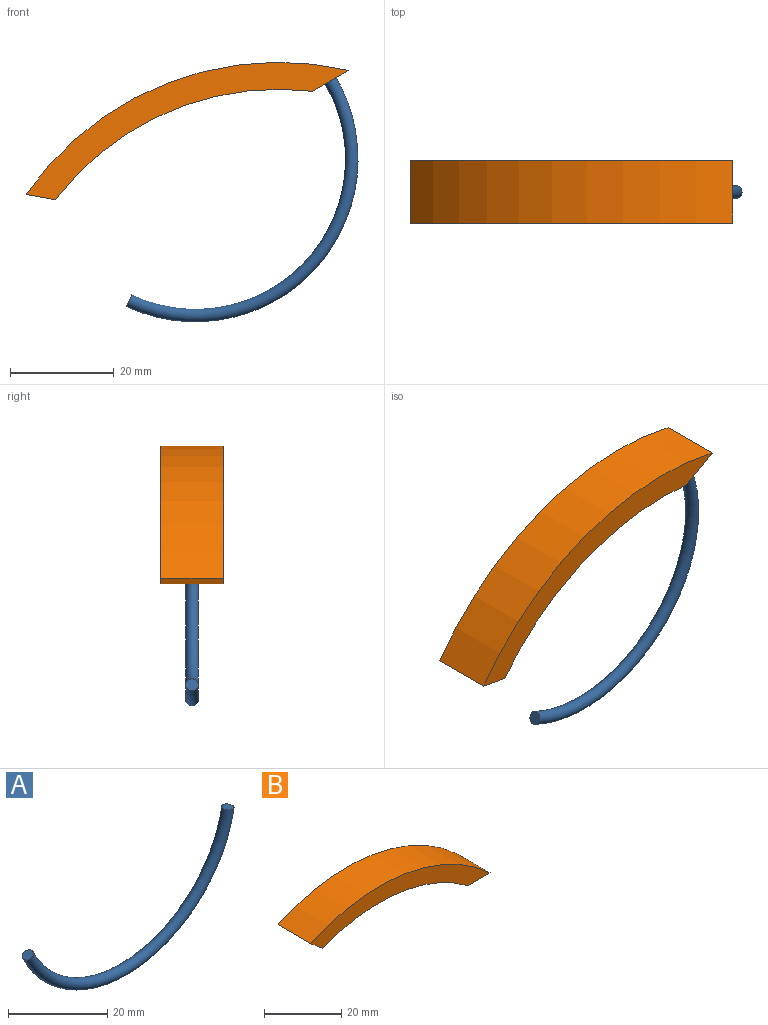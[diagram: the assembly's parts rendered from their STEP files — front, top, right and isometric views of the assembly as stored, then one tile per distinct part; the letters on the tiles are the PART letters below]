
ASSEMBLY  parts=2 mates=1
PART A: 3 faces, bbox 64.1x2.5x29.2 mm
  f0: plane 2.5x2.26mm, normal (-0.43,0,0.9), area 4.9mm2, adj f2
  f1: plane 2.5x2.47mm, normal (0.16,0,0.99), area 4.9mm2, adj f2
  f2: torus R=30.09mm, axis (0,-1,0), area 598.4mm2, adj f0,f1
PART B: 6 faces, bbox 65.8x12x16.1 mm
  f0: cylinder r=54.02mm len=53.31mm, axis (0,1,0), area 674.9mm2, adj f1,f3,f4,f5
  f1: plane 12x8.05mm, normal (0,0,-1), area 96.6mm2, adj f0,f2,f4,f5
  f2: cylinder r=59.21mm len=65.76mm, axis (0,1,0), area 848.5mm2, adj f1,f3,f4,f5
  f3: plane 12x4.4mm, normal (-0.65,0,-0.76), area 69.2mm2, adj f0,f2,f4,f5
  f4: plane 65.76x16.06mm, normal (0,-1,0), area 330mm2, adj f0,f1,f2,f3
  f5: plane 65.76x16.06mm, normal (0,1,0), area 330mm2, adj f0,f1,f2,f3
PLACE A rot(axis=(0,-1,0),39.5deg) t=(79.14,29.47,38.53)mm
PLACE B rot(axis=(0,-1,0),30deg) t=(19.39,35.47,3.97)mm
MATE fastened A.f1 <-> B.f1  axis (-0.5,0,0.87) through (79.14,29.47,38.53)mm
